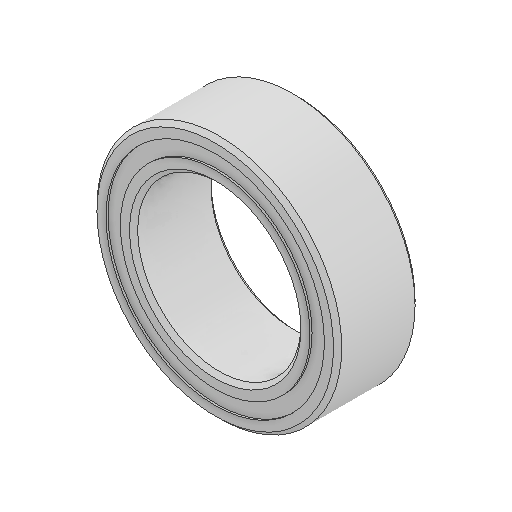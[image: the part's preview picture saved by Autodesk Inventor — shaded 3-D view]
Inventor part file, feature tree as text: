
AUTODESK INVENTOR PART (.ipt)
format: ipt  version: 2024.1 (Build 281209000, 209)  size: 591,872 bytes
history: native  units: in
note: dims shown in document units (in); Inventor stores cm internally (conversion verified against a paired STEP export)
features: other x11, revolve x5
ambient origin geometry x8: Origin, YZ Plane, XZ Plane, XY Plane, X Axis, Y Axis, Z Axis, Center Point
bodies: Solid1 (feature_tree), Solid2 (feature_tree), Solid3 (feature_tree), Solid4 (feature_tree), Solid5 (feature_tree), Solid6 (feature_tree), Solid7 (feature_tree), Solid8 (feature_tree), Solid9 (feature_tree), Solid10 (feature_tree), Solid11 (feature_tree), Solid12 (feature_tree), Solid13 (feature_tree), Solid14 (feature_tree), Solid15 (feature_tree), Solid16 (feature_tree)
feature tree (16):
  revolve  "Revolve1"  [1 undecoded]
  revolve  "Revolve3"  [1 undecoded]
  revolve  "Revolve4"  [1 undecoded]
  other  "CirPattern1[1]"
  other  "CirPattern1[2]"
  other  "CirPattern1[3]"
  other  "CirPattern1[4]"
  other  "CirPattern1[5]"
  other  "CirPattern1[6]"
  other  "CirPattern1[7]"
  other  "CirPattern1[8]"
  other  "CirPattern1[9]"
  other  "CirPattern1[10]"
  other  "CirPattern1[11]"
  revolve  "Revolve5[1]"  [1 undecoded]
  revolve  "Revolve5[2]"  [1 undecoded]
note: 5 required parameter values undecoded (feature->parameter linkage not recoverable at this tier; creation-order binding heuristic only, values carry confidence <= 0.55)
